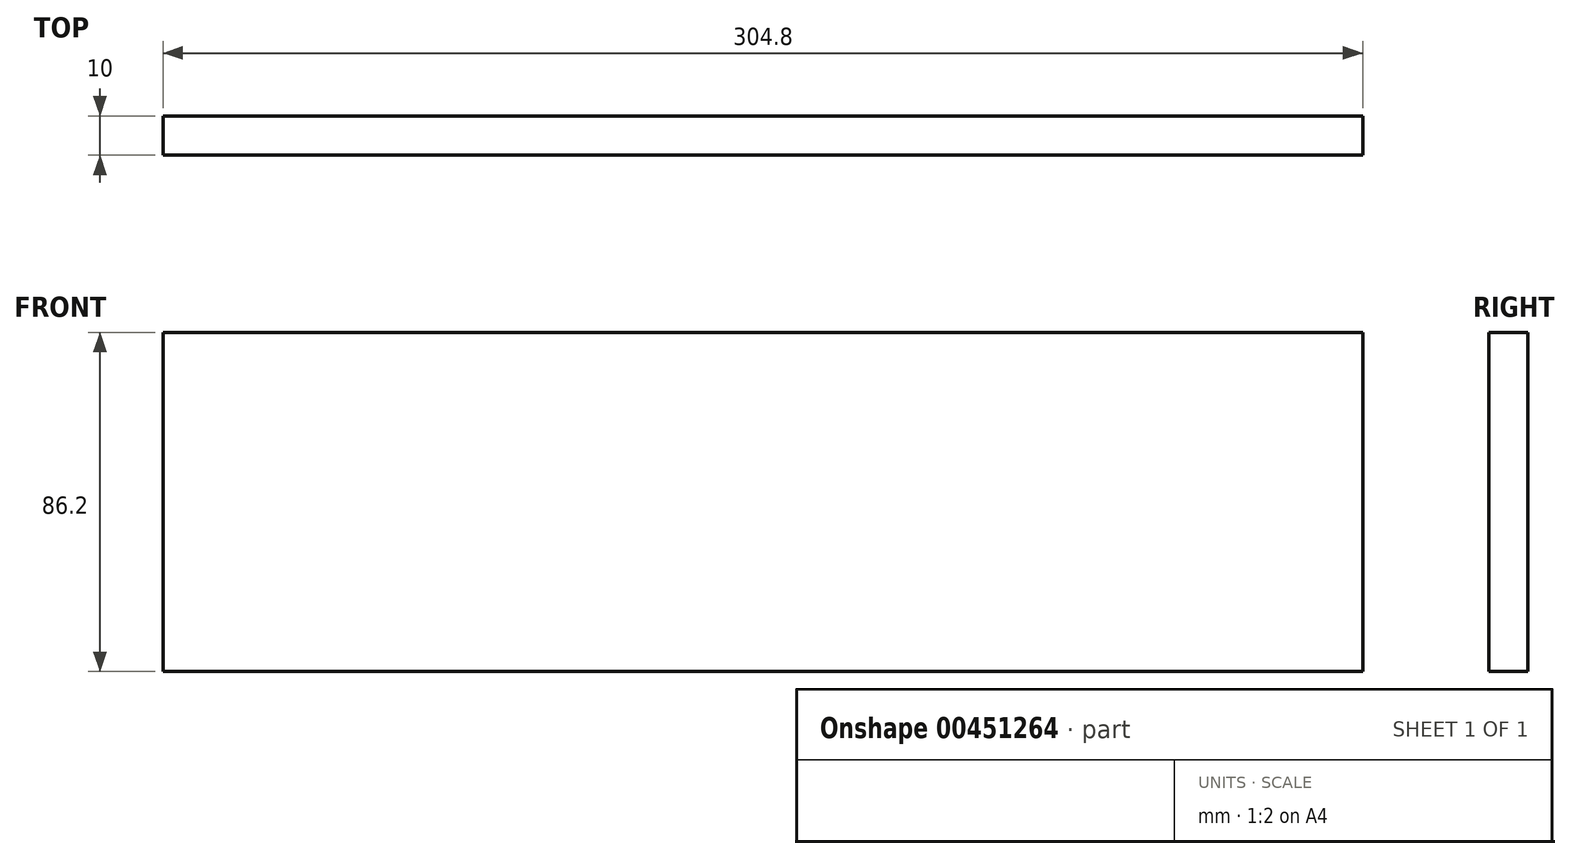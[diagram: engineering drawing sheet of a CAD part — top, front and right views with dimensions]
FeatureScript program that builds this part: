
annotation { "Feature Type Name" : "Feature", "Feature Type Description" : "" }
export const myFeature = defineFeature(function(context is Context, id is Id, definition is map)
    precondition{}
    {
        {
            var Q0;
            Q0=qCreatedBy(makeId("Front.planeOp"),FACE);
            var sketch = newSketch(context, id + "F0", { "sketchPlane" : qUnion([Q0])});
            skLineSegment(sketch, "E0.bottom", {"start": v(152.4, -43.1) * mm, "end": v(-152.4, -43.1) * mm});
            skLineSegment(sketch, "E0.top", {"start": v(152.4, 43.1) * mm, "end": v(-152.4, 43.1) * mm});
            skLineSegment(sketch, "E0.left", {"start": v(152.4, -43.1) * mm, "end": v(152.4, 43.1) * mm});
            skLineSegment(sketch, "E0.right", {"start": v(-152.4, -43.1) * mm, "end": v(-152.4, 43.1) * mm});
            skPoint(sketch, "E0.middle", {"position": v(0, 0) * mm});
            skSolve(sketch);
        }
        {
            var Q0;
            Q0=makeQuery(id+"F0.imprint","IMPRINT",FACE,{"disambiguationData":[TD([[makeQuery(id+"F0.imprint","IMPRINT",EDGE,{"derivedFrom":sQuery(id+"F0.wireOp",EDGE,"E0.bottom")}),-1.0]])]});
            extrude(context, id + "F1", {"entities" : qUnion([Q0]), "depth" : 10 * mm});
        }
    });
